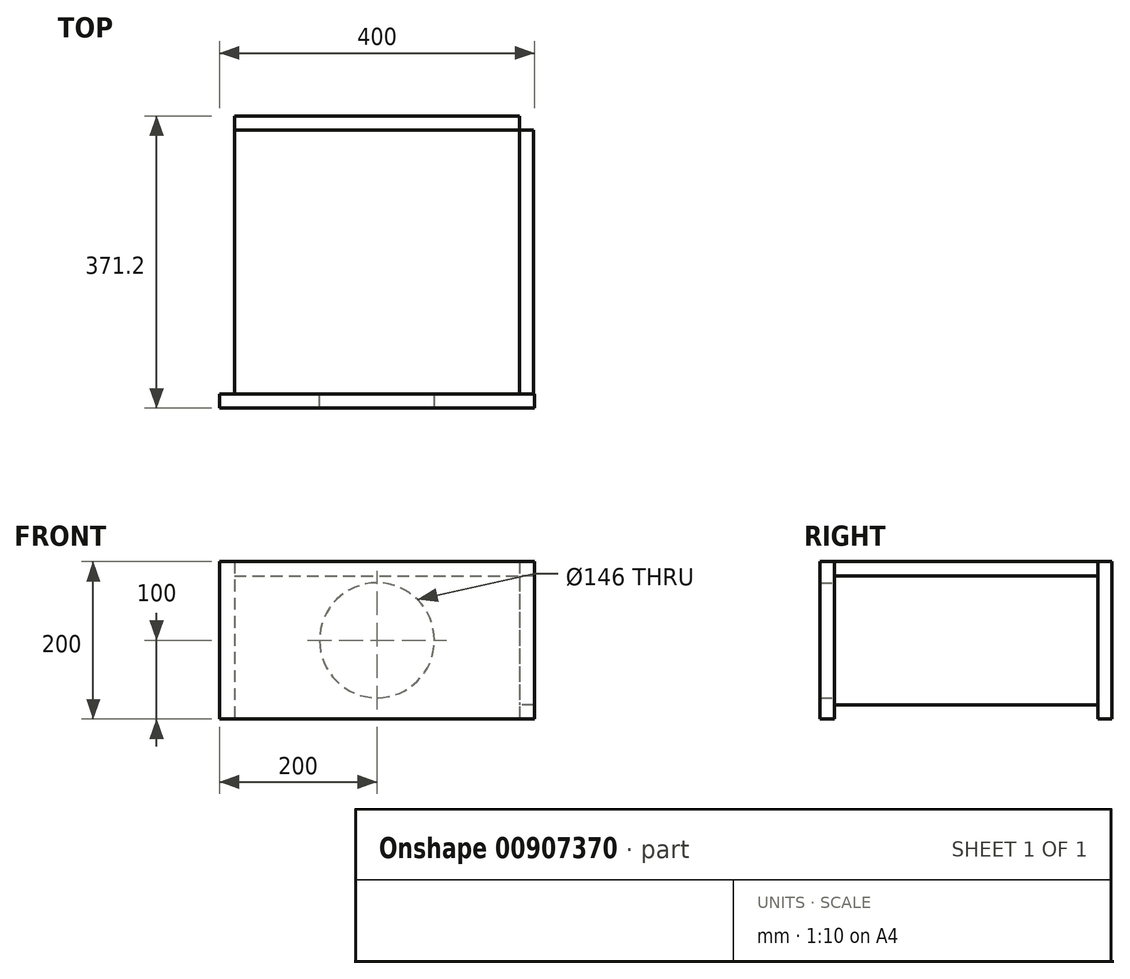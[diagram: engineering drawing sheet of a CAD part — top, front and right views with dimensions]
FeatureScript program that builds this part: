
annotation { "Feature Type Name" : "Feature", "Feature Type Description" : "" }
export const myFeature = defineFeature(function(context is Context, id is Id, definition is map)
    precondition{}
    {
        {
            var Q0;
            Q0=qCreatedBy(makeId("Front.planeOp"),FACE);
            var sketch = newSketch(context, id + "F0", { "sketchPlane" : qUnion([Q0])});
            skLineSegment(sketch, "E0.bottom", {"start": v(200, -100) * mm, "end": v(-200, -100) * mm});
            skLineSegment(sketch, "E0.top", {"start": v(200, 100) * mm, "end": v(-200, 100) * mm});
            skLineSegment(sketch, "E0.left", {"start": v(200, -100) * mm, "end": v(200, 100) * mm});
            skLineSegment(sketch, "E0.right", {"start": v(-200, -100) * mm, "end": v(-200, 100) * mm});
            skPoint(sketch, "E0.middle", {"position": v(0, 0) * mm});
            skCircle(sketch, "E1", {"center": v(0, 0) * mm, "radius": 73 * mm});
            skSolve(sketch);
        }
        {
            var Q0;
            Q0 = qSketchRegion(id + "F0", true);
            extrude(context, id + "F1", {"entities" : qUnion([Q0]), "depth" : 18 * mm, "offsetDistance" : 25 * mm});
        }
        {
            var Q0;
            Q0=makeQuery(id+"F1.opExtrude","CAP_FACE",FACE,{"disambiguationData":[OSD([sQuery(id+"F0.wireOp",EDGE,"E0.bottom"),sQuery(id+"F0.wireOp",EDGE,"E0.top"),sQuery(id+"F0.wireOp",EDGE,"E0.left"),sQuery(id+"F0.wireOp",EDGE,"E0.right"),sQuery(id+"F0.wireOp",EDGE,"E1")])],"isStart":true});
            var sketch = newSketch(context, id + "F2", { "sketchPlane" : qUnion([Q0])});
            skLineSegment(sketch, "E2.bottom", {"start": v(181, 100) * mm, "end": v(-181, 100) * mm});
            skLineSegment(sketch, "E2.top", {"start": v(181, 82) * mm, "end": v(-181, 82) * mm});
            skLineSegment(sketch, "E2.left", {"start": v(181, 100) * mm, "end": v(181, 82) * mm});
            skLineSegment(sketch, "E2.right", {"start": v(-181, 100) * mm, "end": v(-181, 82) * mm});
            skPoint(sketch, "E2.middle", {"position": v(0, 91) * mm});
            skPoint(sketch, "E2.middle.positionSnap0", {"position": v(0, 100) * mm});
            skPoint(sketch, "E2.centerSnap0", {"position": v(0, 100) * mm});
            skSolve(sketch);
        }
        {
            var Q0;
            Q0 = qSketchRegion(id + "F2", true);
            extrude(context, id + "F3", {"entities" : qUnion([Q0]), "depth" : 335 * mm, "offsetDistance" : 25 * mm});
        }
        {
            var Q0;
            Q0=makeQuery(id+"F3.opExtrude","SWEPT_FACE",FACE,{"disambiguationData":[OSD([sQuery(id+"F2.wireOp",EDGE,"E2.right")])]});
            var sketch = newSketch(context, id + "F4", { "sketchPlane" : qUnion([Q0])});
            skLineSegment(sketch, "E3.bottom", {"start": v(0, 82) * mm, "end": v(335, 82) * mm});
            skLineSegment(sketch, "E3.top", {"start": v(0, -82) * mm, "end": v(335, -82) * mm});
            skLineSegment(sketch, "E3.left", {"start": v(0, 82) * mm, "end": v(0, -82) * mm});
            skLineSegment(sketch, "E3.right", {"start": v(335, 82) * mm, "end": v(335, -82) * mm});
            skSolve(sketch);
        }
        {
            var Q0;
            Q0 = qSketchRegion(id + "F4", true);
            extrude(context, id + "F5", {"entities" : qUnion([Q0]), "depth" : 18 * mm, "offsetDistance" : 25 * mm});
        }
        {
            var Q0;
            Q0=makeQuery(id+"F3.opExtrude","CAP_FACE",FACE,{"disambiguationData":[OSD([sQuery(id+"F2.wireOp",EDGE,"E2.bottom"),sQuery(id+"F2.wireOp",EDGE,"E2.top"),sQuery(id+"F2.wireOp",EDGE,"E2.left"),sQuery(id+"F2.wireOp",EDGE,"E2.right")])],"isStart":false});
            var sketch = newSketch(context, id + "F6", { "sketchPlane" : qUnion([Q0])});
            skLineSegment(sketch, "E4.bottom", {"start": v(-181, 100) * mm, "end": v(181, 100) * mm});
            skLineSegment(sketch, "E4.top", {"start": v(-181, -100) * mm, "end": v(181, -100) * mm});
            skLineSegment(sketch, "E4.left", {"start": v(-181, 100) * mm, "end": v(-181, -100) * mm});
            skLineSegment(sketch, "E4.right", {"start": v(181, 100) * mm, "end": v(181, -100) * mm});
            skSolve(sketch);
        }
        {
            var Q0;
            Q0 = qSketchRegion(id + "F6", true);
            extrude(context, id + "F7", {"entities" : qUnion([Q0]), "depth" : 18 * mm, "offsetDistance" : 25 * mm});
        }
        {
            var Q0;
            Q0=makeQuery(id+"F1.opExtrude","CAP_FACE",FACE,{"disambiguationData":[OSD([sQuery(id+"F0.wireOp",EDGE,"E0.bottom"),sQuery(id+"F0.wireOp",EDGE,"E0.top"),sQuery(id+"F0.wireOp",EDGE,"E0.left"),sQuery(id+"F0.wireOp",EDGE,"E0.right"),sQuery(id+"F0.wireOp",EDGE,"E1")])],"isStart":false});
            var sketch = newSketch(context, id + "F8", { "sketchPlane" : qUnion([Q0])});
            skLineSegment(sketch, "E5.bottom", {"start": v(-200, 100) * mm, "end": v(200, 100) * mm});
            skLineSegment(sketch, "E5.top", {"start": v(-200, -100) * mm, "end": v(200, -100) * mm});
            skLineSegment(sketch, "E5.left", {"start": v(-200, 100) * mm, "end": v(-200, -100) * mm});
            skLineSegment(sketch, "E5.right", {"start": v(200, 100) * mm, "end": v(200, -100) * mm});
            skSolve(sketch);
        }
        {
            var Q0;
            Q0 = qSketchRegion(id + "F8", true);
            extrude(context, id + "F9", {"entities" : qUnion([Q0]), "depth" : 0.2 * mm, "offsetDistance" : 25 * mm});
        }
    });
